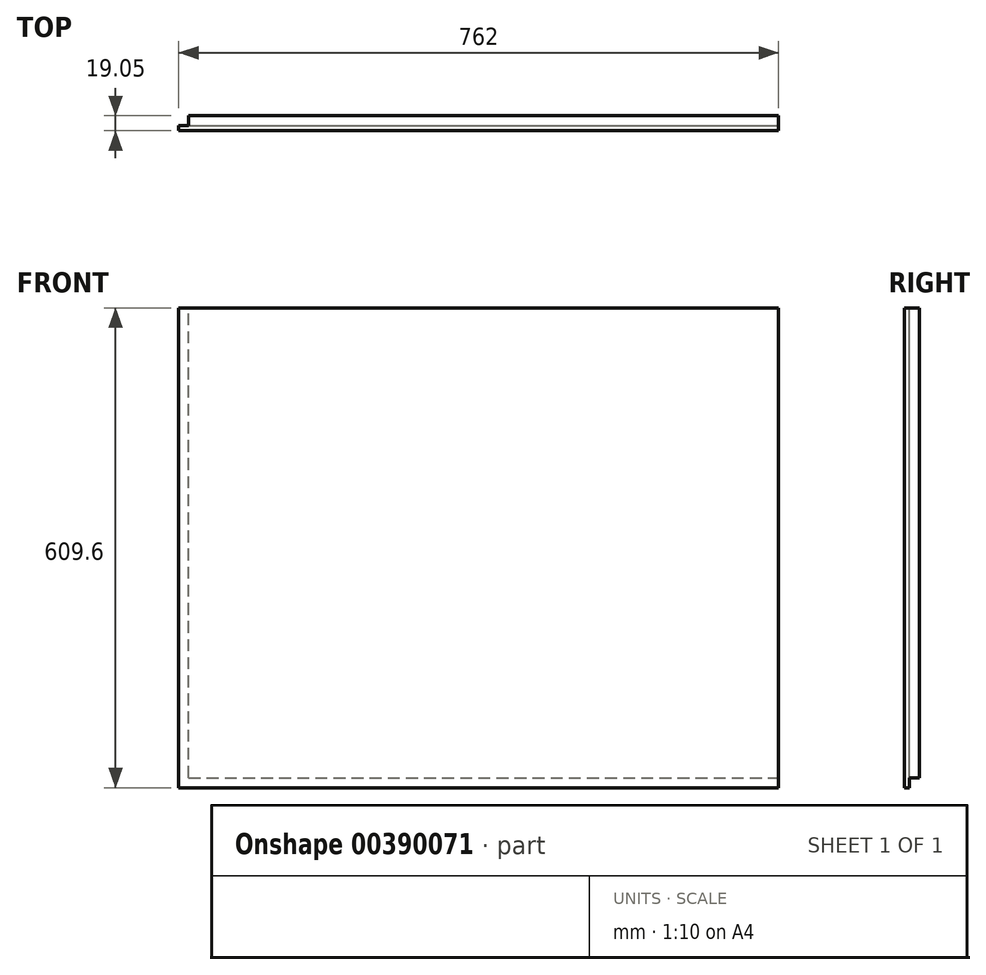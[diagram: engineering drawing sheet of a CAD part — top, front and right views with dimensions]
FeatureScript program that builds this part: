
annotation { "Feature Type Name" : "Feature", "Feature Type Description" : "" }
export const myFeature = defineFeature(function(context is Context, id is Id, definition is map)
    precondition{}
    {
        {
            var Q0;
            Q0=qCreatedBy(makeId("Front.planeOp"),FACE);
            var sketch = newSketch(context, id + "F0", { "sketchPlane" : qUnion([Q0])});
            skLineSegment(sketch, "E0", {"start": v(0, 0) * mm, "end": v(762, 0) * mm});
            skLineSegment(sketch, "E1", {"start": v(762, 0) * mm, "end": v(762, 609.6) * mm});
            skLineSegment(sketch, "E2", {"start": v(762, 609.6) * mm, "end": v(0, 609.6) * mm});
            skLineSegment(sketch, "E3", {"start": v(0, 609.6) * mm, "end": v(0, 0) * mm});
            skSolve(sketch);
        }
        {
            var Q0;
            Q0 = qSketchRegion(id + "F0", true);
            var Q1;
            Q1=makeQuery(id+"F0.imprint","IMPRINT",FACE,{"disambiguationData":[TD([[makeQuery(id+"F0.imprint","IMPRINT",EDGE,{"derivedFrom":sQuery(id+"F0.wireOp",EDGE,"E0")}),1.0]])]});
            extrude(context, id + "F1", {"entities" : qUnion([Q0, Q1]), "depth" : 19.05 * mm});
        }
        {
            var Q0;
            Q0=makeQuery(id+"F1.opExtrude","SWEPT_FACE",FACE,{"disambiguationData":[OSD([sQuery(id+"F0.wireOp",EDGE,"E1")])]});
            var sketch = newSketch(context, id + "F2", { "sketchPlane" : qUnion([Q0])});
            skLineSegment(sketch, "E4", {"start": v(0, 0) * mm, "end": v(-12.7, 0) * mm});
            skLineSegment(sketch, "E5", {"start": v(-12.7, 0) * mm, "end": v(-12.7, 12.7) * mm});
            skLineSegment(sketch, "E6", {"start": v(-12.7, 12.7) * mm, "end": v(0, 12.7) * mm});
            skLineSegment(sketch, "E7", {"start": v(0, 12.7) * mm, "end": v(0, 0) * mm});
            skSolve(sketch);
        }
        {
            var Q0;
            Q0=makeQuery(id+"F2.imprint","IMPRINT",FACE,{"disambiguationData":[TD([[makeQuery(id+"F2.imprint","IMPRINT",EDGE,{"derivedFrom":sQuery(id+"F2.wireOp",EDGE,"E4")}),1.0]])]});
            extrude(context, id + "F3", {"entities" : qUnion([Q0]), "operationType" : NewBodyOperationType.REMOVE, "endBound" : BoundingType.THROUGH_ALL, "oppositeDirection" : true, "depth" : 25.4 * mm});
        }
        {
            var Q0;
            Q0=makeQuery(id+"F1.opExtrude","SWEPT_FACE",FACE,{"disambiguationData":[OSD([sQuery(id+"F0.wireOp",EDGE,"E2")])]});
            var sketch = newSketch(context, id + "F4", { "sketchPlane" : qUnion([Q0])});
            skLineSegment(sketch, "E8", {"start": v(0, 0) * mm, "end": v(0, -12.7) * mm});
            skLineSegment(sketch, "E9", {"start": v(0, -12.7) * mm, "end": v(12.7, -12.7) * mm});
            skLineSegment(sketch, "E10", {"start": v(12.7, -12.7) * mm, "end": v(12.7, 0) * mm});
            skLineSegment(sketch, "E11", {"start": v(12.7, 0) * mm, "end": v(0, 0) * mm});
            skSolve(sketch);
        }
        {
            var Q0;
            Q0 = qSketchRegion(id + "F4", true);
            extrude(context, id + "F5", {"entities" : qUnion([Q0]), "operationType" : NewBodyOperationType.REMOVE, "endBound" : BoundingType.THROUGH_ALL, "oppositeDirection" : true, "depth" : 25.4 * mm});
        }
    });
